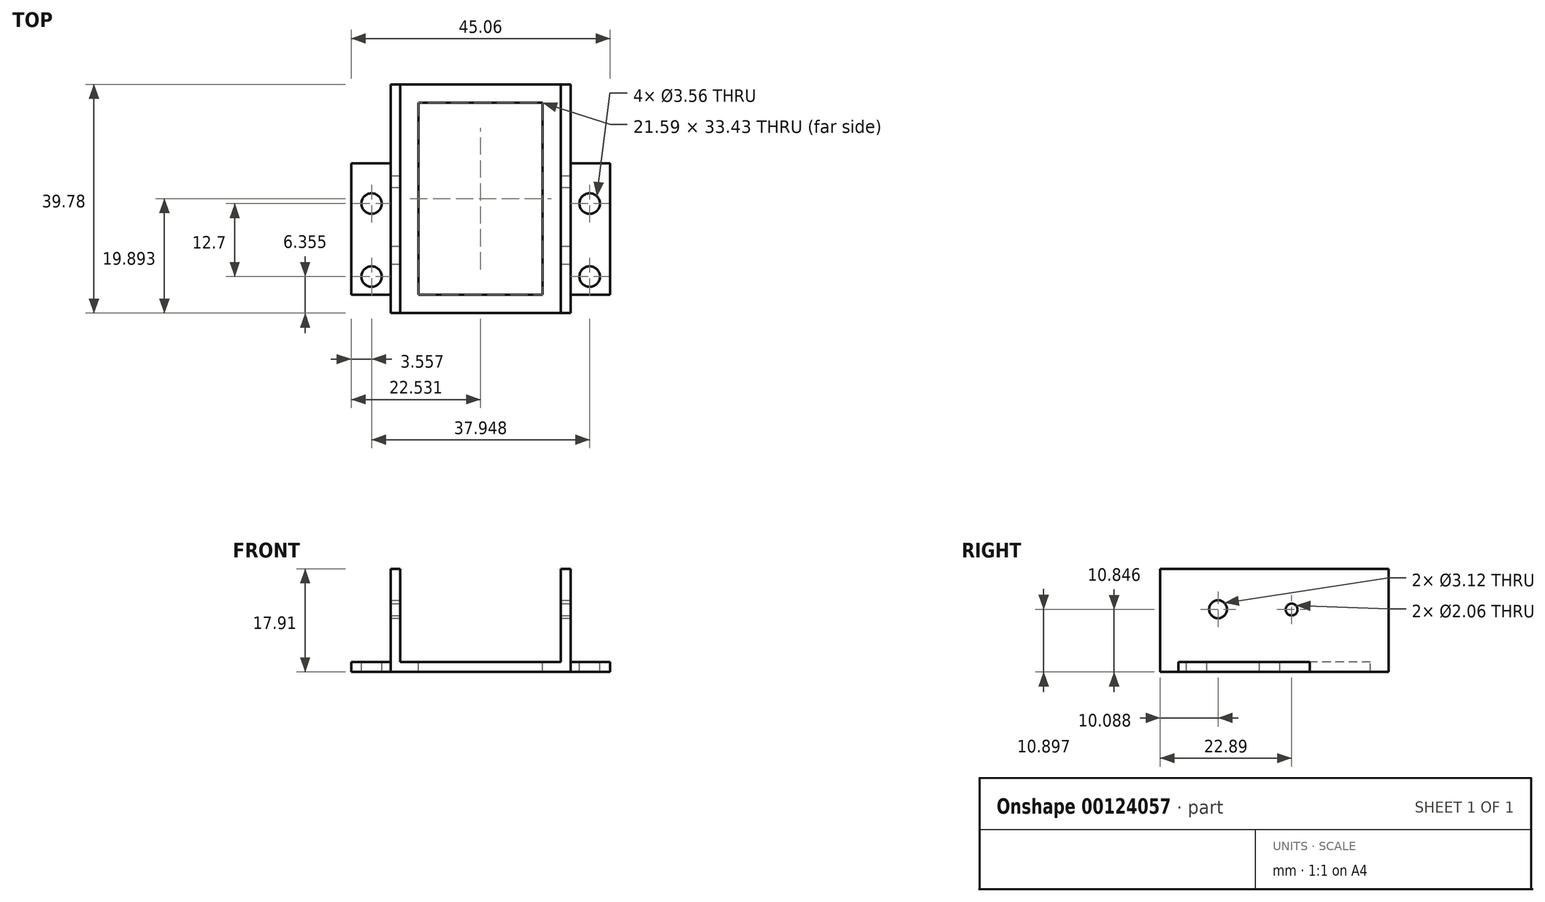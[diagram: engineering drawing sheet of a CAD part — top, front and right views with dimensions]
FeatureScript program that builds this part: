
annotation { "Feature Type Name" : "Feature", "Feature Type Description" : "" }
export const myFeature = defineFeature(function(context is Context, id is Id, definition is map)
    precondition{}
    {
        {
            var Q0;
            Q0=qCreatedBy(makeId("Top.planeOp"),FACE);
            var sketch = newSketch(context, id + "F0", { "sketchPlane" : qUnion([Q0])});
            skLineSegment(sketch, "E0.bottom", {"start": v(-16.08, 32.04) * mm, "end": v(15.26, 32.04) * mm});
            skLineSegment(sketch, "E0.top", {"start": v(-16.08, -7.74) * mm, "end": v(15.26, -7.74) * mm});
            skLineSegment(sketch, "E0.left", {"start": v(-16.08, 32.04) * mm, "end": v(-16.08, -7.74) * mm});
            skLineSegment(sketch, "E0.right", {"start": v(15.26, 32.04) * mm, "end": v(15.26, -7.74) * mm});
            skSolve(sketch);
        }
        {
            var Q0;
            Q0=makeQuery(id+"F0.imprint","IMPRINT",FACE,{"disambiguationData":[TD([[makeQuery(id+"F0.imprint","IMPRINT",EDGE,{"derivedFrom":sQuery(id+"F0.wireOp",EDGE,"E0.bottom")}),-1.0]])]});
            extrude(context, id + "F1", {"entities" : qUnion([Q0]), "depth" : 17.9 * mm});
        }
        {
            var Q0;
            Q0=makeQuery(id+"F1.opExtrude","CAP_FACE",FACE,{"disambiguationData":[OSD([sQuery(id+"F0.wireOp",EDGE,"E0.bottom"),sQuery(id+"F0.wireOp",EDGE,"E0.top"),sQuery(id+"F0.wireOp",EDGE,"E0.left"),sQuery(id+"F0.wireOp",EDGE,"E0.right")])],"isStart":false});
            var sketch = newSketch(context, id + "F2", { "sketchPlane" : qUnion([Q0])});
            skLineSegment(sketch, "E1.bottom", {"start": v(-14.38, 38.04) * mm, "end": v(13.56, 38.04) * mm});
            skLineSegment(sketch, "E1.top", {"start": v(-14.38, -12.76) * mm, "end": v(13.56, -12.76) * mm});
            skLineSegment(sketch, "E1.left", {"start": v(-14.38, 38.04) * mm, "end": v(-14.38, -12.76) * mm});
            skLineSegment(sketch, "E1.right", {"start": v(13.56, 38.04) * mm, "end": v(13.56, -12.76) * mm});
            skSolve(sketch);
        }
        {
            var Q0;
            {var subQ0=sQuery(id+"F2.wireOp",EDGE,"E1.left");var subQ1=makeQuery(id+"F1.opExtrude","CAP_EDGE",EDGE,{"disambiguationData":[OSD([sQuery(id+"F0.wireOp",EDGE,"E0.bottom")])],"isStart":false});var subQ2=makeQuery(id+"F2.imprint","INTERSECT",VERTEX,{"derivedFrom":[subQ1,subQ0]});Q0=makeQuery(id+"F2.imprint","IMPRINT",FACE,{"disambiguationData":[TD([[makeQuery(id+"F2.imprint","IMPRINT",EDGE,{"disambiguationData":[TD([[subQ2,-1.0]])],"derivedFrom":subQ0}),1.0]])]});}
            extrude(context, id + "F3", {"entities" : qUnion([Q0]), "operationType" : NewBodyOperationType.REMOVE, "oppositeDirection" : true, "depth" : 16.2 * mm});
        }
        {
            var Q0;
            Q0=makeQuery(id+"F1.opExtrude","SWEPT_FACE",FACE,{"disambiguationData":[OSD([sQuery(id+"F0.wireOp",EDGE,"E0.left")])]});
            var sketch = newSketch(context, id + "F4", { "sketchPlane" : qUnion([Q0])});
            skLineSegment(sketch, "E2.bottom", {"start": v(-18.3, 1.7) * mm, "end": v(4.56, 1.7) * mm});
            skLineSegment(sketch, "E2.top", {"start": v(-18.3, 0) * mm, "end": v(4.56, 0) * mm});
            skLineSegment(sketch, "E2.left", {"start": v(-18.3, 1.7) * mm, "end": v(-18.3, 0) * mm});
            skLineSegment(sketch, "E2.right", {"start": v(4.56, 1.7) * mm, "end": v(4.56, 0) * mm});
            skSolve(sketch);
        }
        {
            var Q0;
            Q0=makeQuery(id+"F4.imprint","IMPRINT",FACE,{"disambiguationData":[TD([[makeQuery(id+"F4.imprint","IMPRINT",EDGE,{"derivedFrom":sQuery(id+"F4.wireOp",EDGE,"E2.bottom")}),-1.0]])]});
            extrude(context, id + "F5", {"entities" : qUnion([Q0]), "operationType" : NewBodyOperationType.ADD, "depth" : 6.86 * mm});
        }
        {
            var Q0;
            Q0=makeQuery(id+"F1.opExtrude","SWEPT_FACE",FACE,{"disambiguationData":[OSD([sQuery(id+"F0.wireOp",EDGE,"E0.right")])]});
            var sketch = newSketch(context, id + "F6", { "sketchPlane" : qUnion([Q0])});
            skLineSegment(sketch, "E3.bottom", {"start": v(-4.56, 1.7) * mm, "end": v(18.3, 1.7) * mm});
            skLineSegment(sketch, "E3.top", {"start": v(-4.56, 0) * mm, "end": v(18.3, 0) * mm});
            skLineSegment(sketch, "E3.left", {"start": v(-4.56, 1.7) * mm, "end": v(-4.56, 0) * mm});
            skLineSegment(sketch, "E3.right", {"start": v(18.3, 1.7) * mm, "end": v(18.3, 0) * mm});
            skSolve(sketch);
        }
        {
            var Q0;
            Q0=makeQuery(id+"F6.imprint","IMPRINT",FACE,{"disambiguationData":[TD([[makeQuery(id+"F6.imprint","IMPRINT",EDGE,{"derivedFrom":sQuery(id+"F6.wireOp",EDGE,"E3.bottom")}),-1.0]])]});
            extrude(context, id + "F7", {"entities" : qUnion([Q0]), "operationType" : NewBodyOperationType.ADD, "depth" : 6.86 * mm});
        }
        {
            var Q0;
            Q0=makeQuery(id+"F5.opExtrude","SWEPT_FACE",FACE,{"disambiguationData":[OSD([sQuery(id+"F4.wireOp",EDGE,"E2.bottom")])]});
            var sketch = newSketch(context, id + "F8", { "sketchPlane" : qUnion([Q0])});
            skPoint(sketch, "E4", {"position": v(-19.38, -1.39) * mm});
            skPoint(sketch, "E5", {"position": v(18.56, -1.39) * mm});
            skPoint(sketch, "E6", {"position": v(18.56, 11.31) * mm});
            skPoint(sketch, "E7", {"position": v(-19.38, 11.31) * mm});
            skSolve(sketch);
        }
        {
            var Q0;
            Q0=sQuery(id+"F8.wireOp",VERTEX,"E4");
            var Q1;
            Q1=sQuery(id+"F8.wireOp",VERTEX,"E5");
            var Q2;
            Q2=sQuery(id+"F8.wireOp",VERTEX,"E6");
            var Q3;
            Q3=sQuery(id+"F8.wireOp",VERTEX,"E7");
            var Q4;
            Q4=makeQuery(id+"F1.opExtrude","SWEPT_BODY",BODY,{"disambiguationData":[OSD([sQuery(id+"F0.wireOp",EDGE,"E0.bottom"),sQuery(id+"F0.wireOp",EDGE,"E0.top"),sQuery(id+"F0.wireOp",EDGE,"E0.left"),sQuery(id+"F0.wireOp",EDGE,"E0.right")])]});
            hole(context, id + "F9", {"style" : HoleStyle.SIMPLE, "endStyle" : HoleEndStyle.THROUGH, "holeDiameter" : 3.56 * mm, "locations" : qUnion([Q0, Q1, Q2, Q3]), "scope" : qUnion([Q4]), "isTappedThrough" : true});
        }
        {
            var Q0;
            Q0=makeQuery(id+"F1.opExtrude","SWEPT_FACE",FACE,{"disambiguationData":[OSD([sQuery(id+"F0.wireOp",EDGE,"E0.right")])]});
            var sketch = newSketch(context, id + "F10", { "sketchPlane" : qUnion([Q0])});
            skPoint(sketch, "E8", {"position": v(2.35, 10.9) * mm});
            skSolve(sketch);
        }
        {
            var Q0;
            Q0=sQuery(id+"F10.wireOp",VERTEX,"E8");
            var Q1;
            Q1=makeQuery(id+"F1.opExtrude","SWEPT_BODY",BODY,{"disambiguationData":[OSD([sQuery(id+"F0.wireOp",EDGE,"E0.bottom"),sQuery(id+"F0.wireOp",EDGE,"E0.top"),sQuery(id+"F0.wireOp",EDGE,"E0.left"),sQuery(id+"F0.wireOp",EDGE,"E0.right")])]});
            hole(context, id + "F11", {"style" : HoleStyle.SIMPLE, "endStyle" : HoleEndStyle.THROUGH, "holeDiameter" : 3.12 * mm, "locations" : qUnion([Q0]), "scope" : qUnion([Q1]), "isTappedThrough" : true});
        }
        {
            var Q0;
            Q0=makeQuery(id+"F1.opExtrude","SWEPT_FACE",FACE,{"disambiguationData":[OSD([sQuery(id+"F0.wireOp",EDGE,"E0.right")])]});
            var sketch = newSketch(context, id + "F12", { "sketchPlane" : qUnion([Q0])});
            skPoint(sketch, "E9", {"position": v(15.15, 10.85) * mm});
            skPoint(sketch, "E10", {"position": v(2.35, 10.9) * mm});
            skSolve(sketch);
        }
        {
            var Q0;
            Q0=sQuery(id+"F12.wireOp",VERTEX,"E9");
            var Q1;
            Q1=makeQuery(id+"F1.opExtrude","SWEPT_BODY",BODY,{"disambiguationData":[OSD([sQuery(id+"F0.wireOp",EDGE,"E0.bottom"),sQuery(id+"F0.wireOp",EDGE,"E0.top"),sQuery(id+"F0.wireOp",EDGE,"E0.left"),sQuery(id+"F0.wireOp",EDGE,"E0.right")])]});
            hole(context, id + "F13", {"style" : HoleStyle.SIMPLE, "endStyle" : HoleEndStyle.THROUGH, "holeDiameter" : 2.06 * mm, "locations" : qUnion([Q0]), "scope" : qUnion([Q1]), "isTappedThrough" : true});
        }
        {
            var Q0;
            Q0=makeQuery(id+"F3.boolean.opBoolean","COPY",FACE,{"derivedFrom":makeQuery(id+"F3.opExtrude","CAP_FACE",FACE,{"disambiguationData":[OSD([sQuery(id+"F0.wireOp",EDGE,"E0.bottom"),sQuery(id+"F0.wireOp",EDGE,"E0.top"),sQuery(id+"F2.wireOp",EDGE,"E1.left"),sQuery(id+"F2.wireOp",EDGE,"E1.right")])],"isStart":false})});
            var sketch = newSketch(context, id + "F14", { "sketchPlane" : qUnion([Q0])});
            skLineSegment(sketch, "E11.bottom", {"start": v(-11.2, 28.87) * mm, "end": v(10.39, 28.87) * mm});
            skLineSegment(sketch, "E11.top", {"start": v(-11.2, -4.56) * mm, "end": v(10.39, -4.56) * mm});
            skLineSegment(sketch, "E11.left", {"start": v(-11.2, 28.87) * mm, "end": v(-11.2, -4.56) * mm});
            skLineSegment(sketch, "E11.right", {"start": v(10.39, 28.87) * mm, "end": v(10.39, -4.56) * mm});
            skSolve(sketch);
        }
        {
            var Q0;
            Q0=makeQuery(id+"F14.imprint","IMPRINT",FACE,{"disambiguationData":[TD([[makeQuery(id+"F14.imprint","IMPRINT",EDGE,{"derivedFrom":sQuery(id+"F14.wireOp",EDGE,"E11.bottom")}),-1.0]])]});
            extrude(context, id + "F15", {"entities" : qUnion([Q0]), "operationType" : NewBodyOperationType.REMOVE, "oppositeDirection" : true, "depth" : 25.4 * mm});
        }
    });
